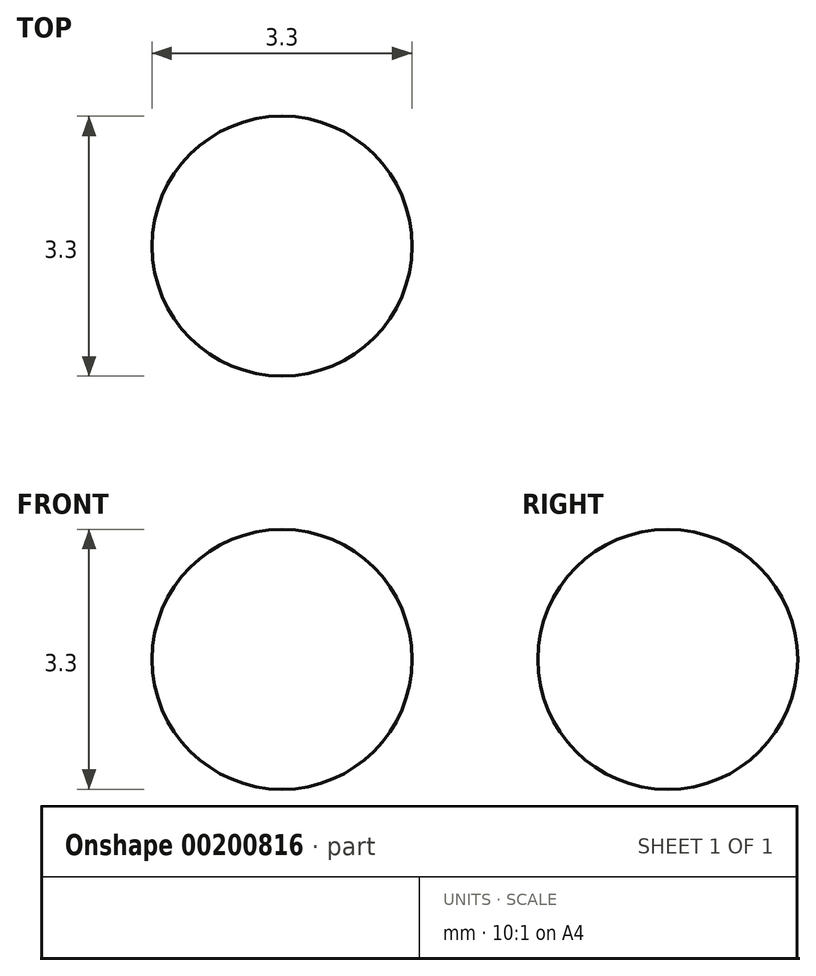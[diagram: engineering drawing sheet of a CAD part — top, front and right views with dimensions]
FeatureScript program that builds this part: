
annotation { "Feature Type Name" : "Feature", "Feature Type Description" : "" }
export const myFeature = defineFeature(function(context is Context, id is Id, definition is map)
    precondition{}
    {
        {
            var Q0;
            Q0=qCreatedBy(makeId("Front.planeOp"),FACE);
            var sketch = newSketch(context, id + "F0", { "sketchPlane" : qUnion([Q0])});
            skArc(sketch, "E0", {"start": v(0, -1.65) * mm, "mid": v(1.65, 0) * mm, "end": v(0, 1.65) * mm});
            skPoint(sketch, "E1", {"position": v(0, 2.8) * mm});
            skPoint(sketch, "E2", {"position": v(0, -3.13) * mm});
            skLineSegment(sketch, "E3", {"start": v(0, 2.8) * mm, "end": v(0, -3.13) * mm, "construction": true});
            skLineSegment(sketch, "E4", {"start": v(0, 1.65) * mm, "end": v(0, -1.65) * mm});
            skSolve(sketch);
        }
        {
            var Q0;
            Q0=makeQuery(id+"F0.imprint","IMPRINT",FACE,{"disambiguationData":[TD([[makeQuery(id+"F0.imprint","IMPRINT",EDGE,{"derivedFrom":sQuery(id+"F0.wireOp",EDGE,"E0")}),1.0]])]});
            var Q1;
            Q1=sQuery(id+"F0.wireOp",EDGE,"E4");
            revolve(context, id + "F1", {"entities" : qUnion([Q0]), "axis" : qUnion([Q1]), "revolveType" : RevolveType.FULL});
        }
    });
